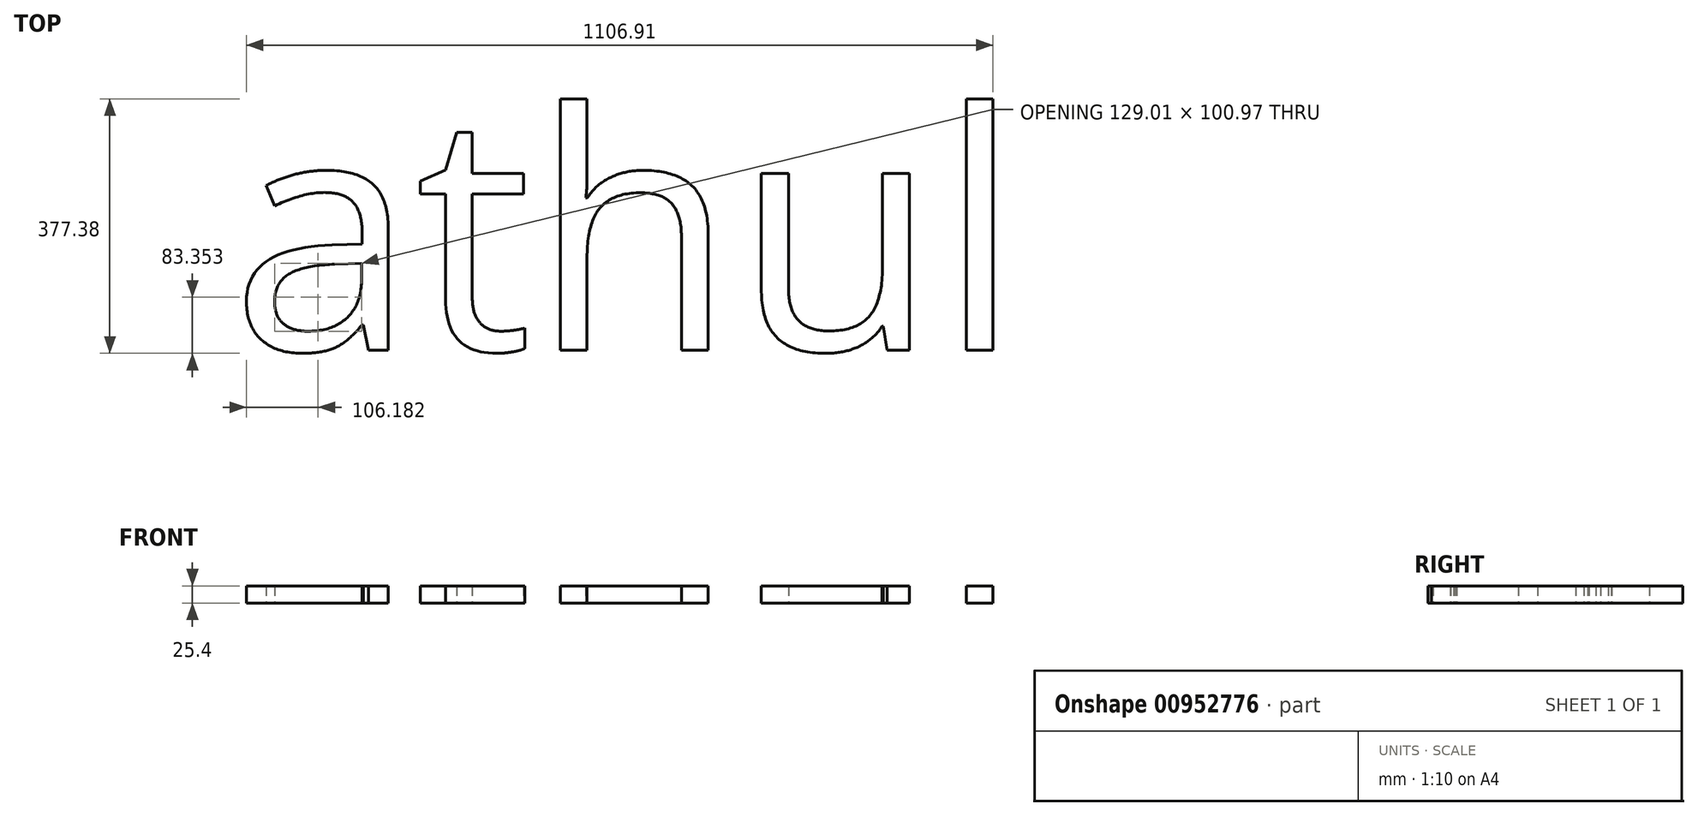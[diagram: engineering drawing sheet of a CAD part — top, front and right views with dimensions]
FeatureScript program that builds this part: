
annotation { "Feature Type Name" : "Feature", "Feature Type Description" : "" }
export const myFeature = defineFeature(function(context is Context, id is Id, definition is map)
    precondition{}
    {
        {
            var Q0;
            Q0=qCreatedBy(makeId("Top.planeOp"),FACE);
            var sketch = newSketch(context, id + "F0", { "sketchPlane" : qUnion([Q0])});
            skText(sketch, "E0", { "text": "athul", "fontName": "OpenSans-Regular.ttf"});
            const initialGuessF0  = {"E0": [-0.21771, -0.42598, 1, 0, 0.35301]};
            skSetInitialGuess(sketch, initialGuessF0);
            skSolve(sketch);
        }
        {
            var Q0;
            Q0 = qSketchRegion(id + "F0", true);
            extrude(context, id + "F1", {"entities" : qUnion([Q0]), "depth" : 25.4 * mm, "offsetDistance" : 25.4 * mm});
        }
    });
